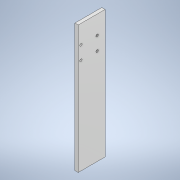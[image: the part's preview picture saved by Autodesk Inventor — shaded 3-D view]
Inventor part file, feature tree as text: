
AUTODESK INVENTOR PART (.ipt)
format: ipt  version: 2022 (Build 260153000, 153)  size: 118,784 bytes
history: native  units: mm
features: sketch x2, other x1, extrude x1, hole x1
ambient origin geometry x8: Origin, YZ Plane, XZ Plane, XY Plane, X Axis, Y Axis, Z Axis, Center Point
bodies: Body1 (feature_tree)
feature tree (5):
  other  "ソリッド1"
  extrude  "押し出し1"  Depth=40.0mm
  hole  "穴1"  [1 undecoded]
  sketch  "スケッチ1"
  sketch  "スケッチ2"
note: 1 required parameter value undecoded (feature->parameter linkage not recoverable at this tier; creation-order binding heuristic only, values carry confidence <= 0.55)
